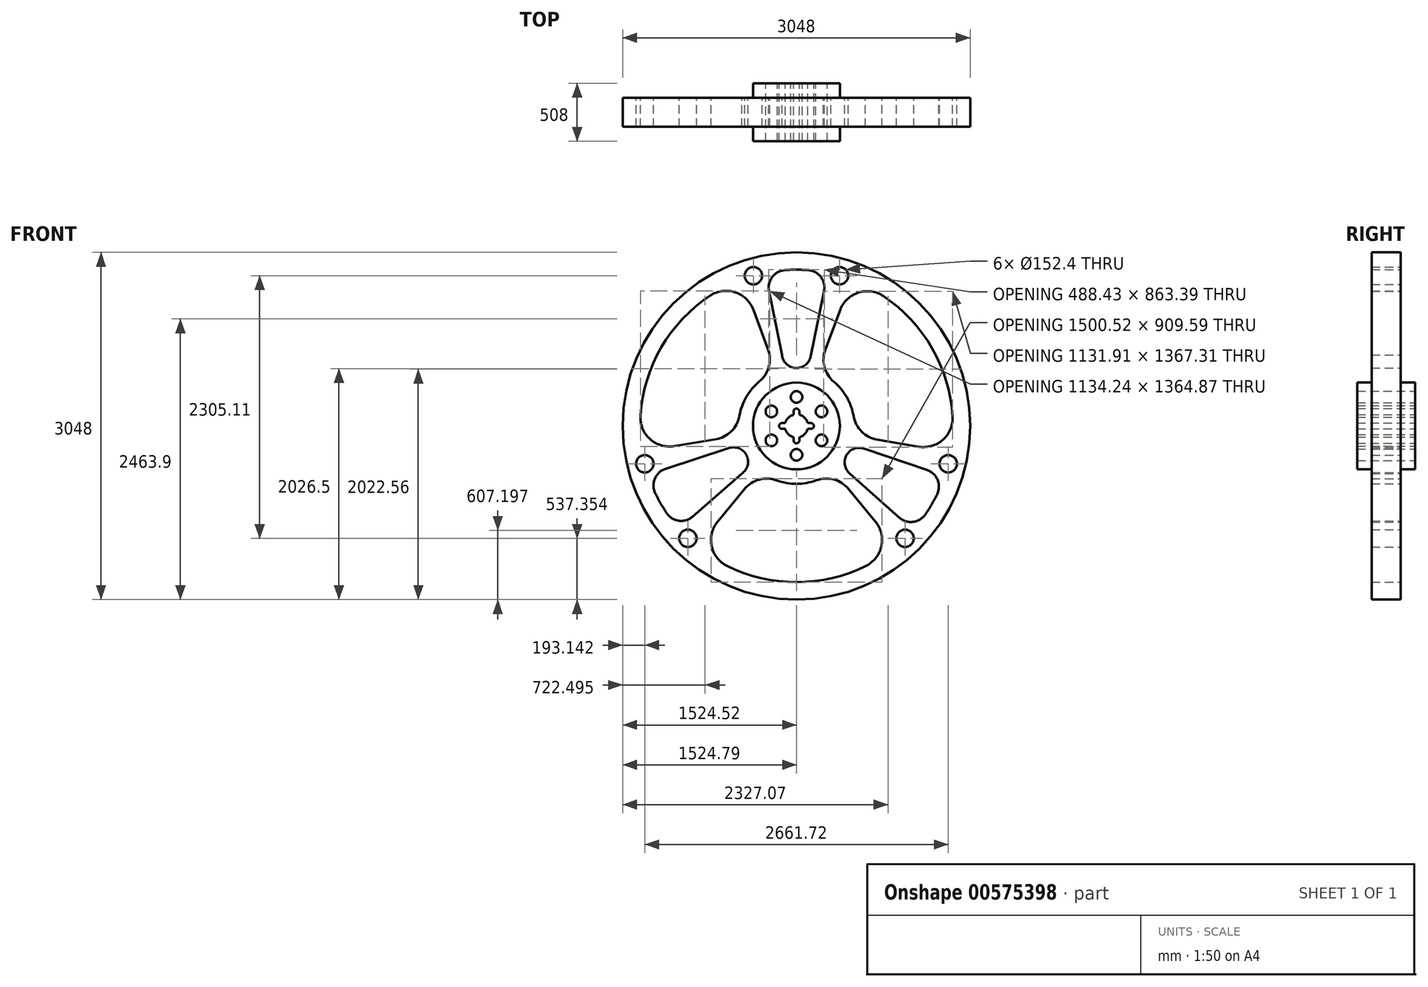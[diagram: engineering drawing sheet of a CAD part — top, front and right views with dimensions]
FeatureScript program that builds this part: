
annotation { "Feature Type Name" : "Feature", "Feature Type Description" : "" }
export const myFeature = defineFeature(function(context is Context, id is Id, definition is map)
    precondition{}
    {
        {
            var Q0;
            Q0=qCreatedBy(makeId("Front.planeOp"),FACE);
            var sketch = newSketch(context, id + "F0", { "sketchPlane" : qUnion([Q0])});
            skCircle(sketch, "E0", {"center": v(0, 0) * mm, "radius": 1524 * mm});
            skArc(sketch, "E1", {"start": v(-608.44, -1229.27) * mm, "mid": v(0.72, -1371.6) * mm, "end": v(609.72, -1228.63) * mm});
            skCircle(sketch, "E2", {"center": v(-378.06, 1318.47) * mm, "radius": 76.2 * mm});
            skCircle(sketch, "E3", {"center": v(378.06, 1318.47) * mm, "radius": 76.2 * mm});
            skCircle(sketch, "E4.1.0", {"center": v(-952.8, -986.65) * mm, "radius": 76.2 * mm});
            skCircle(sketch, "E4.1.1", {"center": v(-1330.86, -331.82) * mm, "radius": 76.2 * mm});
            skCircle(sketch, "E4.2.0", {"center": v(1330.86, -331.82) * mm, "radius": 76.2 * mm});
            skCircle(sketch, "E4.2.1", {"center": v(952.8, -986.65) * mm, "radius": 76.2 * mm});
            skLineSegment(sketch, "E5", {"start": v(457.26, -554.11) * mm, "end": v(692.72, -839.44) * mm});
            skLineSegment(sketch, "E6", {"start": v(-120.85, 595.95) * mm, "end": v(-240.4, 1185.5) * mm});
            skLineSegment(sketch, "E7", {"start": v(124.43, 609.6) * mm, "end": v(241.93, 1185.2) * mm});
            skArc(sketch, "E8", {"start": v(-325.4, 390.1) * mm, "mid": v(-439.33, 255.06) * mm, "end": v(-500.11, 89.17) * mm});
            skArc(sketch, "E9", {"start": v(-126.51, 623.9) * mm, "mid": v(-7.22, 508.2) * mm, "end": v(124.43, 609.6) * mm});
            skArc(sketch, "E10", {"start": v(-479.38, -418.86) * mm, "mid": v(-437.94, -257.94) * mm, "end": v(-591.23, -193.77) * mm});
            skLineSegment(sketch, "E11.trimOffspring", {"start": v(-591.23, -193.77) * mm, "end": v(-1149.48, -376.72) * mm});
            skLineSegment(sketch, "E12.trimOffspring", {"start": v(-457.9, -400.1) * mm, "end": v(-910.9, -795.91) * mm});
            skArc(sketch, "E13", {"start": v(-173.74, -477.37) * mm, "mid": v(-327.48, -471.01) * mm, "end": v(-456.68, -554.59) * mm});
            skArc(sketch, "E14", {"start": v(457.26, -554.11) * mm, "mid": v(327.97, -470.67) * mm, "end": v(174.24, -477.19) * mm});
            skArc(sketch, "E15", {"start": v(-691.84, -840.16) * mm, "mid": v(-744.12, -1054.86) * mm, "end": v(-608.44, -1229.27) * mm});
            skArc(sketch, "E16", {"start": v(609.72, -1228.63) * mm, "mid": v(745.22, -1054.08) * mm, "end": v(692.72, -839.44) * mm});
            skArc(sketch, "E17", {"start": v(-325.4, 390.1) * mm, "mid": v(-242.64, 519.83) * mm, "end": v(-249.97, 673.53) * mm});
            skArc(sketch, "E18", {"start": v(-378.69, 1020.35) * mm, "mid": v(-538.03, 1173.44) * mm, "end": v(-757, 1143.78) * mm});
            skArc(sketch, "E19", {"start": v(-708.85, -116.86) * mm, "mid": v(-571.74, -47.02) * mm, "end": v(-500.11, 89.17) * mm});
            skArc(sketch, "E20", {"start": v(-1368.62, 90.3) * mm, "mid": v(-1285.81, -114.56) * mm, "end": v(-1073.86, -177.04) * mm});
            skLineSegment(sketch, "E21.trimOffspring", {"start": v(-249.97, 673.53) * mm, "end": v(-378.69, 1020.35) * mm});
            skLineSegment(sketch, "E22.trimOffspring", {"start": v(-708.85, -116.86) * mm, "end": v(-1073.86, -177.04) * mm});
            skArc(sketch, "E23.trimOffspring", {"start": v(-173.74, -477.37) * mm, "mid": v(0.27, -508) * mm, "end": v(174.24, -477.19) * mm});
            skArc(sketch, "E24", {"start": v(253.04, 672.38) * mm, "mid": v(245.01, 518.72) * mm, "end": v(327.18, 388.61) * mm});
            skArc(sketch, "E25", {"start": v(1073.04, -181.94) * mm, "mid": v(1285.28, -120.43) * mm, "end": v(1369.02, 84.05) * mm});
            skArc(sketch, "E26", {"start": v(500.51, 86.89) * mm, "mid": v(571.52, -49.63) * mm, "end": v(708.31, -120.1) * mm});
            skArc(sketch, "E27", {"start": v(762.21, 1140.31) * mm, "mid": v(543.38, 1170.97) * mm, "end": v(383.34, 1018.6) * mm});
            skArc(sketch, "E28.trimOffspring", {"start": v(-757, 1143.78) * mm, "mid": v(-1186.18, 688.67) * mm, "end": v(-1368.62, 90.3) * mm});
            skArc(sketch, "E29.trimOffspring", {"start": v(1369.02, 84.05) * mm, "mid": v(1189.31, 683.25) * mm, "end": v(762.21, 1140.31) * mm});
            skArc(sketch, "E30.trimOffspring", {"start": v(500.51, 86.89) * mm, "mid": v(440.49, 253.05) * mm, "end": v(327.18, 388.61) * mm});
            skArc(sketch, "E31", {"start": v(602.97, -204.13) * mm, "mid": v(443.01, -249.13) * mm, "end": v(464.52, -413.9) * mm});
            skLineSegment(sketch, "E32.trimOffspring", {"start": v(575.97, -194.99) * mm, "end": v(1145.76, -387.88) * mm});
            skArc(sketch, "E33", {"start": v(-102.42, 1367.77) * mm, "mid": v(-212.55, 1307.78) * mm, "end": v(-240.4, 1185.5) * mm});
            skArc(sketch, "E34", {"start": v(241.93, 1185.2) * mm, "mid": v(214.23, 1307.5) * mm, "end": v(104.18, 1367.64) * mm});
            skArc(sketch, "E35.trimOffspring", {"start": v(104.18, 1367.64) * mm, "mid": v(0.88, 1371.6) * mm, "end": v(-102.42, 1367.77) * mm});
            skArc(sketch, "E36", {"start": v(-1137.58, -766.3) * mm, "mid": v(-1030.93, -832.26) * mm, "end": v(-910.9, -795.91) * mm});
            skArc(sketch, "E37", {"start": v(-1149.48, -376.72) * mm, "mid": v(-1242.03, -461.35) * mm, "end": v(-1239.77, -586.74) * mm});
            skArc(sketch, "E38.trimOffspring", {"start": v(-1239.77, -586.74) * mm, "mid": v(-1192.06, -678.44) * mm, "end": v(-1137.58, -766.3) * mm});
            skArc(sketch, "E39", {"start": v(1234, -598.76) * mm, "mid": v(1237.48, -473.4) * mm, "end": v(1145.76, -387.88) * mm});
            skArc(sketch, "E40", {"start": v(903.12, -804.73) * mm, "mid": v(1022.78, -842.25) * mm, "end": v(1130.07, -777.32) * mm});
            skArc(sketch, "E41.trimOffspring", {"start": v(1130.07, -777.32) * mm, "mid": v(1185.4, -690) * mm, "end": v(1234, -598.76) * mm});
            skCircle(sketch, "E42", {"center": v(0, 0) * mm, "radius": 381 * mm});
            skCircle(sketch, "E43", {"center": v(0, 254) * mm, "radius": 50.8 * mm});
            skCircle(sketch, "E44", {"center": v(0, -254) * mm, "radius": 50.8 * mm});
            skCircle(sketch, "E45.1.0", {"center": v(-219.97, -127) * mm, "radius": 50.8 * mm});
            skCircle(sketch, "E45.1.1", {"center": v(219.97, 127) * mm, "radius": 50.8 * mm});
            skCircle(sketch, "E45.2.0", {"center": v(219.97, -127) * mm, "radius": 50.8 * mm});
            skCircle(sketch, "E45.2.1", {"center": v(-219.97, 127) * mm, "radius": 50.8 * mm});
            skArc(sketch, "E46.trimOffspring", {"start": v(240.59, -81.45) * mm, "mid": v(240.72, -81.07) * mm, "end": v(240.84, -80.69) * mm});
            skArc(sketch, "E47.trimOffspring", {"start": v(189.64, -168.98) * mm, "mid": v(189.97, -168.6) * mm, "end": v(190.3, -168.23) * mm});
            skArc(sketch, "E48.trimOffspring", {"start": v(-191.27, -167.13) * mm, "mid": v(-190.79, -167.68) * mm, "end": v(-190.3, -168.23) * mm});
            skArc(sketch, "E49.trimOffspring", {"start": v(-241.37, -79.1) * mm, "mid": v(-241.1, -79.9) * mm, "end": v(-240.84, -80.69) * mm});
            skArc(sketch, "E50", {"start": v(-25.4, 98.37) * mm, "mid": v(-71.84, 71.84) * mm, "end": v(-98.37, 25.4) * mm});
            skLineSegment(sketch, "E51.trimOffspring", {"start": v(253.04, 672.38) * mm, "end": v(383.34, 1018.6) * mm});
            skLineSegment(sketch, "E52.trimOffspring", {"start": v(708.31, -120.1) * mm, "end": v(1073.04, -181.94) * mm});
            skLineSegment(sketch, "E53.trimOffspring", {"start": v(-456.68, -554.59) * mm, "end": v(-691.84, -840.16) * mm});
            skLineSegment(sketch, "E54.trimOffspring", {"start": v(-177.85, -155.4) * mm, "end": v(-197.48, -172.55) * mm});
            skLineSegment(sketch, "E55.trimOffspring", {"start": v(226.23, -76.59) * mm, "end": v(245.62, -83.15) * mm});
            skLineSegment(sketch, "E56.trimOffspring", {"start": v(464.52, -413.9) * mm, "end": v(903.12, -804.73) * mm});
            skArc(sketch, "E57", {"start": v(-127, 25.4) * mm, "mid": v(-152.4, 0) * mm, "end": v(-127, -25.4) * mm});
            skLineSegment(sketch, "E58", {"start": v(-127, 25.4) * mm, "end": v(-98.37, 25.4) * mm});
            skLineSegment(sketch, "E59", {"start": v(-127, -25.4) * mm, "end": v(-98.37, -25.4) * mm});
            skArc(sketch, "E60", {"start": v(25.4, 127) * mm, "mid": v(0, 152.4) * mm, "end": v(-25.4, 127) * mm});
            skLineSegment(sketch, "E61", {"start": v(25.4, 127) * mm, "end": v(25.4, 98.37) * mm});
            skLineSegment(sketch, "E62", {"start": v(-25.4, 127) * mm, "end": v(-25.4, 98.37) * mm});
            skArc(sketch, "E63", {"start": v(127, -25.4) * mm, "mid": v(152.4, 0) * mm, "end": v(127, 25.4) * mm});
            skLineSegment(sketch, "E64", {"start": v(127, 25.4) * mm, "end": v(98.37, 25.4) * mm});
            skLineSegment(sketch, "E65", {"start": v(127, -25.4) * mm, "end": v(98.37, -25.4) * mm});
            skArc(sketch, "E66", {"start": v(-25.4, -127) * mm, "mid": v(0, -152.4) * mm, "end": v(25.4, -127) * mm});
            skLineSegment(sketch, "E67", {"start": v(-25.4, -127) * mm, "end": v(-25.4, -98.37) * mm});
            skLineSegment(sketch, "E68", {"start": v(25.4, -127) * mm, "end": v(25.4, -98.37) * mm});
            skArc(sketch, "E69.trimOffspring", {"start": v(98.37, 25.4) * mm, "mid": v(71.84, 71.84) * mm, "end": v(25.4, 98.37) * mm});
            skArc(sketch, "E70.trimOffspring", {"start": v(25.4, -98.37) * mm, "mid": v(71.84, -71.84) * mm, "end": v(98.37, -25.4) * mm});
            skArc(sketch, "E71.trimOffspring", {"start": v(-98.37, -25.4) * mm, "mid": v(-71.84, -71.84) * mm, "end": v(-25.4, -98.37) * mm});
            skPoint(sketch, "E72.start.orphan", {"position": v(0, 152.4) * mm});
            skPoint(sketch, "E73.start.orphan", {"position": v(152.4, 0) * mm});
            skPoint(sketch, "E74.start.orphan", {"position": v(0, -152.4) * mm});
            skPoint(sketch, "E75.start.orphan", {"position": v(-152.4, 0) * mm});
            skSolve(sketch);
        }
        {
            var Q0;
            Q0=makeQuery(id+"F0.imprint","IMPRINT",FACE,{"disambiguationData":[TD([[makeQuery(id+"F0.imprint","IMPRINT",EDGE,{"derivedFrom":sQuery(id+"F0.wireOp",EDGE,"E0")}),1.0]])]});
            extrude(context, id + "F1", {"entities" : qUnion([Q0]), "depth" : 254 * mm, "offsetDistance" : 25.4 * mm, "symmetric" : true});
        }
        {
            var Q0;
            Q0=makeQuery(id+"F0.imprint","IMPRINT",FACE,{"disambiguationData":[TD([[makeQuery(id+"F0.imprint","IMPRINT",EDGE,{"derivedFrom":sQuery(id+"F0.wireOp",EDGE,"E42")}),1.0]])]});
            extrude(context, id + "F2", {"entities" : qUnion([Q0]), "operationType" : NewBodyOperationType.ADD, "depth" : 508 * mm, "offsetDistance" : 25.4 * mm, "symmetric" : true});
        }
    });
